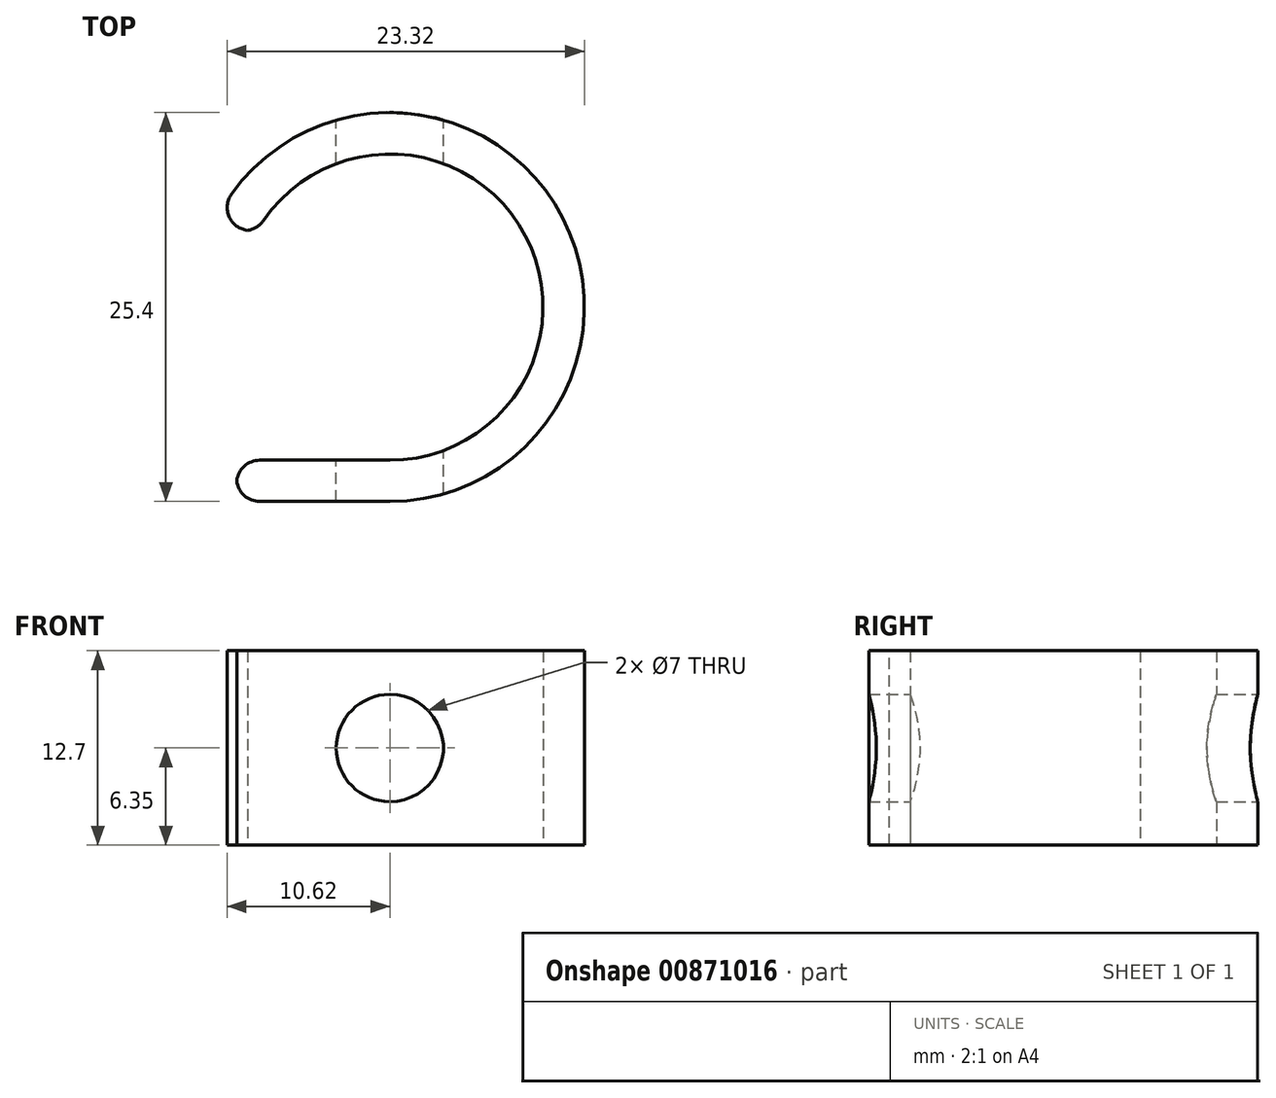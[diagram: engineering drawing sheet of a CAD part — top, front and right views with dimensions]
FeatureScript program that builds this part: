
annotation { "Feature Type Name" : "Feature", "Feature Type Description" : "" }
export const myFeature = defineFeature(function(context is Context, id is Id, definition is map)
    precondition{}
    {
        {
            var Q0;
            Q0=qCreatedBy(makeId("Top.planeOp"),FACE);
            var sketch = newSketch(context, id + "F0", { "sketchPlane" : qUnion([Q0])});
            skCircle(sketch, "E0", {"center": v(0, 0) * mm, "radius": 12.7 * mm});
            skCircle(sketch, "E1", {"center": v(0, 0) * mm, "radius": 10 * mm});
            skLineSegment(sketch, "E2.bottom", {"start": v(0, 0) * mm, "end": v(-21.72, 0) * mm});
            skLineSegment(sketch, "E2.top", {"start": v(0, -15.13) * mm, "end": v(-21.72, -15.13) * mm});
            skLineSegment(sketch, "E2.left", {"start": v(0, 0) * mm, "end": v(0, -15.13) * mm});
            skLineSegment(sketch, "E2.right", {"start": v(-21.72, 0) * mm, "end": v(-21.72, -15.13) * mm});
            skSolve(sketch);
        }
        {
            var Q0;
            {var subQ0=sQuery(id+"F0.wireOp",EDGE,"E2.bottom");var subQ1=sQuery(id+"F0.wireOp",EDGE,"E0");var subQ2=makeQuery(id+"F0.imprint","INTERSECT",VERTEX,{"derivedFrom":[subQ1,subQ0]});Q0=makeQuery(id+"F0.imprint","IMPRINT",FACE,{"disambiguationData":[TD([[makeQuery(id+"F0.imprint","IMPRINT",EDGE,{"disambiguationData":[TD([[subQ2,1.0]])],"derivedFrom":subQ1}),1.0]])]});}
            extrude(context, id + "F1", {"entities" : qUnion([Q0]), "depth" : 12.7 * mm, "offsetDistance" : 25 * mm});
        }
        {
            var Q0;
            Q0=makeQuery(id+"F1.opExtrude","SWEPT_FACE",FACE,{"disambiguationData":[OSD([sQuery(id+"F0.wireOp",EDGE,"E2.left")])]});
            var sketch = newSketch(context, id + "F2", { "sketchPlane" : qUnion([Q0])});
            skLineSegment(sketch, "E3.bottom", {"start": v(10, 0) * mm, "end": v(12.7, 0) * mm});
            skLineSegment(sketch, "E3.top", {"start": v(10, 12.7) * mm, "end": v(12.7, 12.7) * mm});
            skLineSegment(sketch, "E3.left", {"start": v(10, 0) * mm, "end": v(10, 12.7) * mm});
            skLineSegment(sketch, "E3.right", {"start": v(12.7, 0) * mm, "end": v(12.7, 12.7) * mm});
            skSolve(sketch);
        }
        {
            var Q0;
            Q0 = qSketchRegion(id + "F2", true);
            extrude(context, id + "F3", {"entities" : qUnion([Q0]), "operationType" : NewBodyOperationType.ADD, "depth" : 10 * mm, "offsetDistance" : 25 * mm});
        }
        {
            var Q0;
            Q0=makeQuery(id+"F3.opExtrude","SWEPT_FACE",FACE,{"disambiguationData":[OSD([sQuery(id+"F2.wireOp",EDGE,"E3.left")])]});
            var sketch = newSketch(context, id + "F4", { "sketchPlane" : qUnion([Q0])});
            skPoint(sketch, "E4", {"position": v(0, 6.35) * mm});
            skCircle(sketch, "E5", {"center": v(0, 6.35) * mm, "radius": 3.5 * mm});
            skSolve(sketch);
        }
        {
            var Q0;
            Q0 = qSketchRegion(id + "F4", true);
            extrude(context, id + "F5", {"entities" : qUnion([Q0]), "operationType" : NewBodyOperationType.REMOVE, "endBound" : BoundingType.THROUGH_ALL, "oppositeDirection" : true, "depth" : 25 * mm, "offsetDistance" : 25 * mm, "hasSecondDirection" : true, "secondDirectionBound" : BoundingType.THROUGH_ALL, "secondDirectionOppositeDirection" : false, "secondDirectionDepth" : 25 * mm});
        }
        {
            var Q0;
            Q0=makeQuery(id+"F3.opExtrude","CAP_EDGE",EDGE,{"disambiguationData":[OSD([sQuery(id+"F2.wireOp",EDGE,"E3.left")])],"isStart":false});
            var Q1;
            Q1=makeQuery(id+"F3.opExtrude","CAP_EDGE",EDGE,{"disambiguationData":[OSD([sQuery(id+"F2.wireOp",EDGE,"E3.right")])],"isStart":false});
            fillet(context, id + "F6", {"entities" : qUnion([Q0, Q1]), "radius" : 1.5 * mm, "tangentPropagation" : true, "allowEdgeOverflow" : false});
        }
        {
            var Q0;
            Q0=makeQuery(id+"F1.opExtrude","SWEPT_FACE",FACE,{"disambiguationData":[OSD([sQuery(id+"F0.wireOp",EDGE,"E2.bottom")])]});
            var sketch = newSketch(context, id + "F7", { "sketchPlane" : qUnion([Q0])});
            skLineSegment(sketch, "E6.bottom", {"start": v(-17, 14.2) * mm, "end": v(-8.3, 14.2) * mm});
            skLineSegment(sketch, "E6.top", {"start": v(-17, -2.07) * mm, "end": v(-8.3, -2.07) * mm});
            skLineSegment(sketch, "E6.left", {"start": v(-17, 14.2) * mm, "end": v(-17, -2.07) * mm});
            skLineSegment(sketch, "E6.right", {"start": v(-8.3, 14.2) * mm, "end": v(-8.3, -2.07) * mm});
            skSolve(sketch);
        }
        {
            var Q0;
            Q0 = qSketchRegion(id + "F7", true);
            extrude(context, id + "F8", {"entities" : qUnion([Q0]), "operationType" : NewBodyOperationType.REMOVE, "oppositeDirection" : true, "depth" : 5 * mm, "offsetDistance" : 25 * mm});
        }
        {
            var Q0;
            Q0=makeQuery(id+"F8.boolean.opBoolean","INTERSECT",EDGE,{"derivedFrom":[makeQuery(id+"F1.opExtrude","SWEPT_FACE",FACE,{"disambiguationData":[OSD([sQuery(id+"F0.wireOp",EDGE,"E1")])]}),makeQuery(id+"F8.opExtrude","CAP_FACE",FACE,{"disambiguationData":[OSD([sQuery(id+"F7.wireOp",EDGE,"E6.bottom"),sQuery(id+"F7.wireOp",EDGE,"E6.top"),sQuery(id+"F7.wireOp",EDGE,"E6.left"),sQuery(id+"F7.wireOp",EDGE,"E6.right")])],"isStart":false})]});
            var Q1;
            Q1=makeQuery(id+"F8.boolean.opBoolean","INTERSECT",EDGE,{"derivedFrom":[makeQuery(id+"F1.opExtrude","SWEPT_FACE",FACE,{"disambiguationData":[OSD([sQuery(id+"F0.wireOp",EDGE,"E0")])]}),makeQuery(id+"F8.opExtrude","CAP_FACE",FACE,{"disambiguationData":[OSD([sQuery(id+"F7.wireOp",EDGE,"E6.bottom"),sQuery(id+"F7.wireOp",EDGE,"E6.top"),sQuery(id+"F7.wireOp",EDGE,"E6.left"),sQuery(id+"F7.wireOp",EDGE,"E6.right")])],"isStart":false})]});
            fillet(context, id + "F9", {"entities" : qUnion([Q0, Q1]), "radius" : 1.5 * mm, "tangentPropagation" : true, "allowEdgeOverflow" : false});
        }
    });
